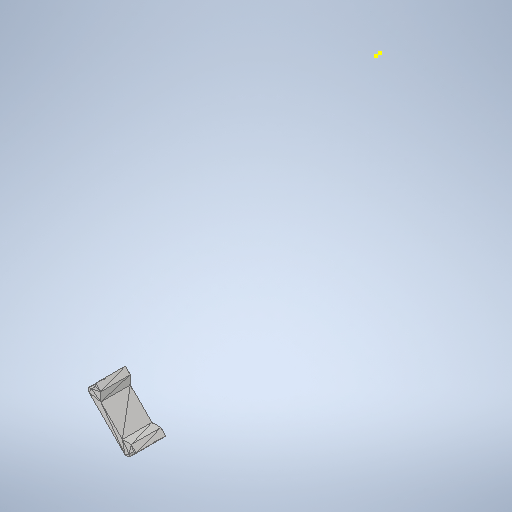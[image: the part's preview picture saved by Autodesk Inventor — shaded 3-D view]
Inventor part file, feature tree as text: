
AUTODESK INVENTOR PART (.ipt)
format: ipt  version: 2025.1 (Build 291241000, 241)  size: 262,144 bytes
history: native  units: mm
features: other x2, sketch x2
ambient origin geometry x8: Origin, YZ Plane, XZ Plane, XY Plane, X Axis, Y Axis, Z Axis, Center Point
feature tree (4):
  other  "20_Cube_Insert_Mirror_Holder_wLogo_v3"
  sketch  "草图1"
  sketch  "草图2"
  other  "网格特征1"
